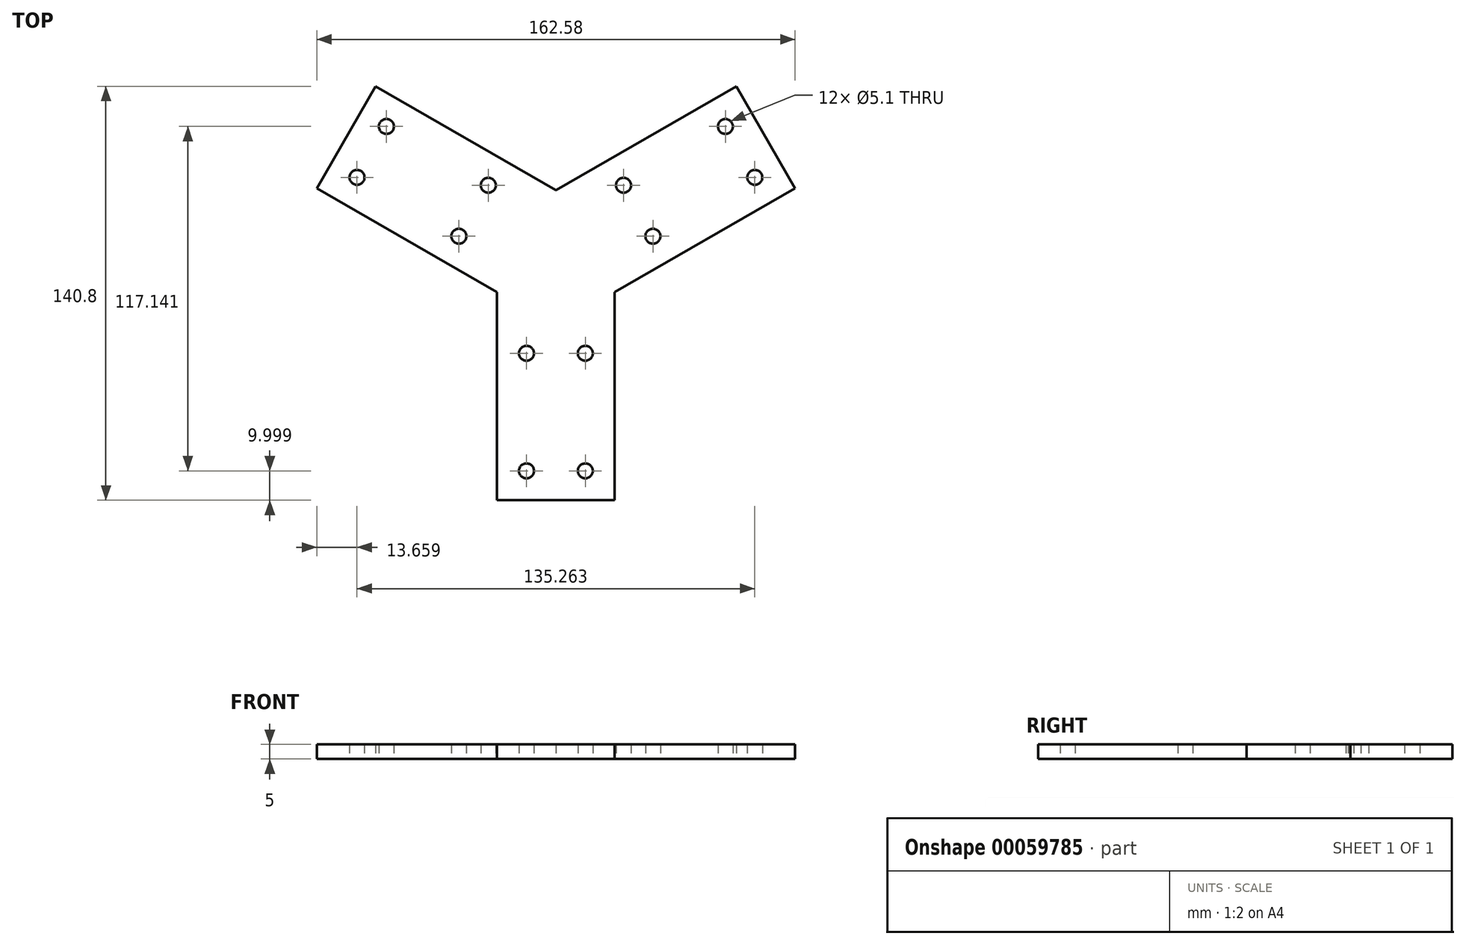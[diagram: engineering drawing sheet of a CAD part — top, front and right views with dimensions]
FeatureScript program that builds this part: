
annotation { "Feature Type Name" : "Feature", "Feature Type Description" : "" }
export const myFeature = defineFeature(function(context is Context, id is Id, definition is map)
    precondition{}
    {
        {
            var Q0;
            Q0=qCreatedBy(makeId("Top.planeOp"),FACE);
            var sketch = newSketch(context, id + "F0", { "sketchPlane" : qUnion([Q0])});
            skLineSegment(sketch, "E0", {"start": v(-30, -17.32) * mm, "end": v(-86.3, 15.18) * mm});
            skLineSegment(sketch, "E1", {"start": v(-86.3, 15.18) * mm, "end": v(-56.3, 67.14) * mm});
            skLineSegment(sketch, "E2", {"start": v(-56.3, 67.14) * mm, "end": v(0, 34.64) * mm});
            skLineSegment(sketch, "E3", {"start": v(0, 34.64) * mm, "end": v(56.3, 67.14) * mm});
            skLineSegment(sketch, "E4", {"start": v(56.3, 67.14) * mm, "end": v(86.3, 15.18) * mm});
            skLineSegment(sketch, "E5", {"start": v(86.3, 15.18) * mm, "end": v(30, -17.32) * mm});
            skLineSegment(sketch, "E6", {"start": v(30, -17.32) * mm, "end": v(30, -82.32) * mm});
            skLineSegment(sketch, "E7", {"start": v(30, -82.32) * mm, "end": v(-30, -82.32) * mm});
            skLineSegment(sketch, "E8", {"start": v(-30, -82.32) * mm, "end": v(-30, -17.32) * mm});
            skLineSegment(sketch, "E9", {"start": v(-30, -17.32) * mm, "end": v(0, 34.64) * mm, "construction": true});
            skLineSegment(sketch, "E10", {"start": v(30, -17.32) * mm, "end": v(0, 34.64) * mm, "construction": true});
            skLineSegment(sketch, "E11", {"start": v(-30, -17.32) * mm, "end": v(30, -17.32) * mm, "construction": true});
            skCircle(sketch, "E12", {"center": v(0, 0) * mm, "radius": 17.32 * mm, "construction": true});
            skLineSegment(sketch, "E13", {"start": v(-30, -82.32) * mm, "end": v(-40, -76.55) * mm});
            skCircle(sketch, "E14", {"center": v(-35, -29.32) * mm, "radius": 2.6 * mm});
            skPoint(sketch, "E14.centerSnap0", {"position": v(-35, -17.32) * mm});
            skCircle(sketch, "E15", {"center": v(-35, -59.32) * mm, "radius": 2.6 * mm});
            skLineSegment(sketch, "E16.1.1", {"start": v(82.83, 13.18) * mm, "end": v(30.87, -16.82) * mm});
            skCircle(sketch, "E16.1.3", {"center": v(42.9, -15.65) * mm, "radius": 2.6 * mm});
            skCircle(sketch, "E16.1.4", {"center": v(68.87, -0.65) * mm, "radius": 2.6 * mm});
            skLineSegment(sketch, "E16.1.5", {"start": v(86.3, 15.18) * mm, "end": v(86.3, 3.63) * mm});
            skLineSegment(sketch, "E16.2.1", {"start": v(-51.96, 64.64) * mm, "end": v(0, 34.64) * mm});
            skCircle(sketch, "E16.2.3", {"center": v(-7.9, 44.97) * mm, "radius": 2.6 * mm});
            skCircle(sketch, "E16.2.4", {"center": v(-33.87, 59.97) * mm, "radius": 2.6 * mm});
            skLineSegment(sketch, "E16.2.5", {"start": v(-56.3, 67.14) * mm, "end": v(-46.3, 72.91) * mm});
            skCircle(sketch, "E17.MirrorC", {"center": v(35, -29.32) * mm, "radius": 2.6 * mm});
            skCircle(sketch, "E18.MirrorC", {"center": v(35, -59.32) * mm, "radius": 2.6 * mm});
            skLineSegment(sketch, "E19.MirrorCS", {"start": v(30, -82.32) * mm, "end": v(40, -76.55) * mm});
            skCircle(sketch, "E20.1.1", {"center": v(33.87, 59.97) * mm, "radius": 2.6 * mm});
            skCircle(sketch, "E20.1.2", {"center": v(7.9, 44.97) * mm, "radius": 2.6 * mm});
            skLineSegment(sketch, "E20.1.3", {"start": v(56.3, 67.14) * mm, "end": v(46.3, 72.91) * mm});
            skCircle(sketch, "E20.2.1", {"center": v(-68.87, -0.65) * mm, "radius": 2.6 * mm});
            skCircle(sketch, "E20.2.2", {"center": v(-42.9, -15.65) * mm, "radius": 2.6 * mm});
            skLineSegment(sketch, "E20.2.3", {"start": v(-86.3, 15.18) * mm, "end": v(-86.3, 3.63) * mm});
            skLineSegment(sketch, "E21", {"start": v(40, -76.55) * mm, "end": v(40, -23.1) * mm});
            skLineSegment(sketch, "E22", {"start": v(86.3, 3.63) * mm, "end": v(40, -23.1) * mm});
            skLineSegment(sketch, "E23", {"start": v(-40, -76.55) * mm, "end": v(-40, -23.1) * mm});
            skLineSegment(sketch, "E24", {"start": v(-86.3, 3.63) * mm, "end": v(-40, -23.1) * mm});
            skLineSegment(sketch, "E25", {"start": v(46.3, 72.91) * mm, "end": v(0, 46.19) * mm});
            skLineSegment(sketch, "E26", {"start": v(-46.3, 72.91) * mm, "end": v(0, 46.19) * mm});
            skLineSegment(sketch, "E27", {"start": v(-20, -82.32) * mm, "end": v(-20, -11.55) * mm});
            skLineSegment(sketch, "E28", {"start": v(-20, -11.55) * mm, "end": v(-81.3, 23.84) * mm});
            skLineSegment(sketch, "E29", {"start": v(20, -82.32) * mm, "end": v(20, -11.55) * mm});
            skLineSegment(sketch, "E30", {"start": v(20, -11.55) * mm, "end": v(81.3, 23.84) * mm});
            skLineSegment(sketch, "E31", {"start": v(61.3, 58.48) * mm, "end": v(0, 23.1) * mm});
            skLineSegment(sketch, "E32", {"start": v(0, 23.1) * mm, "end": v(-61.3, 58.48) * mm});
            skCircle(sketch, "E33", {"center": v(67.63, 27.5) * mm, "radius": 2.55 * mm});
            skCircle(sketch, "E34", {"center": v(57.63, 44.82) * mm, "radius": 2.55 * mm});
            skCircle(sketch, "E35", {"center": v(33, 7.5) * mm, "radius": 2.55 * mm});
            skCircle(sketch, "E36", {"center": v(23, 24.82) * mm, "radius": 2.55 * mm});
            skCircle(sketch, "E37", {"center": v(-23, 24.82) * mm, "radius": 2.55 * mm});
            skCircle(sketch, "E38", {"center": v(-33, 7.5) * mm, "radius": 2.55 * mm});
            skCircle(sketch, "E39", {"center": v(-67.63, 27.5) * mm, "radius": 2.55 * mm});
            skCircle(sketch, "E40", {"center": v(-57.63, 44.82) * mm, "radius": 2.55 * mm});
            skCircle(sketch, "E41", {"center": v(-10, -32.32) * mm, "radius": 2.55 * mm});
            skCircle(sketch, "E42", {"center": v(10, -32.32) * mm, "radius": 2.55 * mm});
            skCircle(sketch, "E43", {"center": v(-10, -72.32) * mm, "radius": 2.55 * mm});
            skCircle(sketch, "E44", {"center": v(10, -72.32) * mm, "radius": 2.55 * mm});
            skSolve(sketch);
        }
        {
            var Q0;
            {var subQ0=sQuery(id+"F0.wireOp",EDGE,"E27");Q0=makeQuery(id+"F0.imprint","IMPRINT",FACE,{"disambiguationData":[TD([[makeQuery(id+"F0.imprint","IMPRINT",EDGE,{"derivedFrom":subQ0}),-1.0]])]});}
            extrude(context, id + "F1", {"entities" : qUnion([Q0]), "depth" : 5 * mm});
        }
    });
